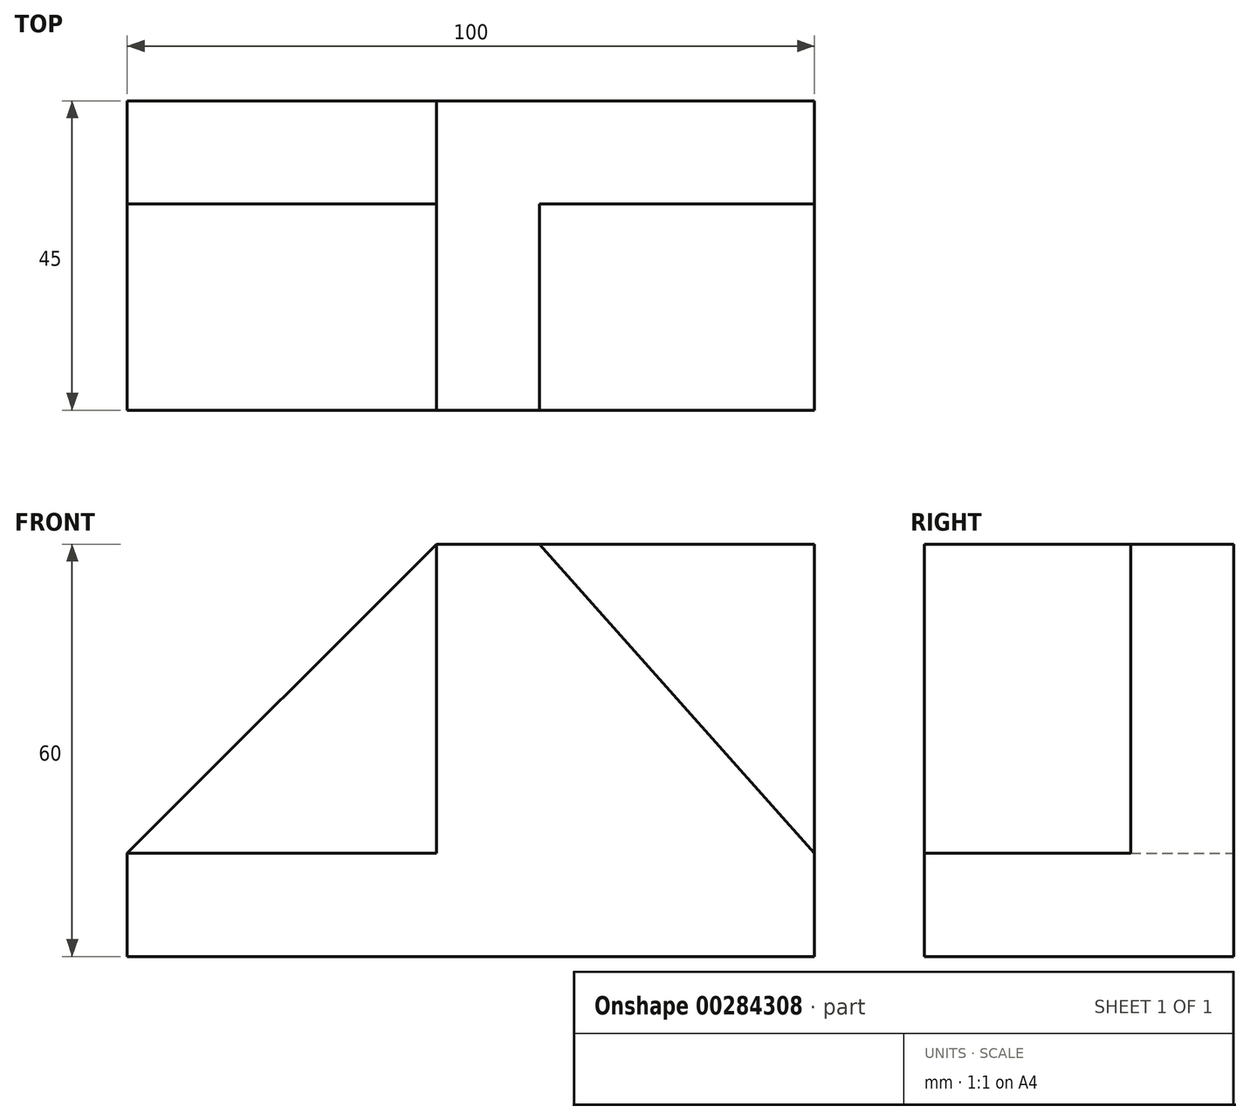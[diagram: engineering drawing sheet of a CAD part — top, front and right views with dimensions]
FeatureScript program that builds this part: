
annotation { "Feature Type Name" : "Feature", "Feature Type Description" : "" }
export const myFeature = defineFeature(function(context is Context, id is Id, definition is map)
    precondition{}
    {
        {
            var Q0;
            Q0=qCreatedBy(makeId("Front.planeOp"),FACE);
            var sketch = newSketch(context, id + "F0", { "sketchPlane" : qUnion([Q0])});
            skLineSegment(sketch, "E0", {"start": v(-62.69, -4.46) * mm, "end": v(-62.69, -19.46) * mm});
            skLineSegment(sketch, "E1", {"start": v(-62.69, -19.46) * mm, "end": v(37.31, -19.46) * mm});
            skLineSegment(sketch, "E2", {"start": v(37.31, -19.46) * mm, "end": v(37.31, -4.46) * mm});
            skLineSegment(sketch, "E3", {"start": v(-17.69, 40.54) * mm, "end": v(-2.69, 40.54) * mm});
            skLineSegment(sketch, "E4", {"start": v(-2.69, 40.54) * mm, "end": v(37.31, 40.54) * mm});
            skLineSegment(sketch, "E5", {"start": v(37.31, 40.54) * mm, "end": v(37.31, -4.46) * mm});
            skLineSegment(sketch, "E6", {"start": v(-62.69, -4.46) * mm, "end": v(-17.69, 40.54) * mm});
            skSolve(sketch);
        }
        {
            var Q0;
            Q0 = qSketchRegion(id + "F0", true);
            extrude(context, id + "F1", {"entities" : qUnion([Q0]), "depth" : 45 * mm});
        }
        {
            var Q0;
            Q0=makeQuery(id+"F1.opExtrude","CAP_FACE",FACE,{"disambiguationData":[OSD([sQuery(id+"F0.wireOp",EDGE,"E0"),sQuery(id+"F0.wireOp",EDGE,"E1"),sQuery(id+"F0.wireOp",EDGE,"E2"),sQuery(id+"F0.wireOp",EDGE,"E3"),sQuery(id+"F0.wireOp",EDGE,"E4"),sQuery(id+"F0.wireOp",EDGE,"E5"),sQuery(id+"F0.wireOp",EDGE,"E6")])],"isStart":false});
            var sketch = newSketch(context, id + "F2", { "sketchPlane" : qUnion([Q0])});
            skLineSegment(sketch, "E7", {"start": v(-17.69, 40.54) * mm, "end": v(-17.69, -4.46) * mm});
            skLineSegment(sketch, "E8", {"start": v(-17.69, -4.46) * mm, "end": v(-62.69, -4.46) * mm});
            skLineSegment(sketch, "E9", {"start": v(-62.69, -4.46) * mm, "end": v(-17.69, 40.54) * mm});
            skSolve(sketch);
        }
        {
            var Q0;
            Q0 = qSketchRegion(id + "F2", true);
            extrude(context, id + "F3", {"entities" : qUnion([Q0]), "operationType" : NewBodyOperationType.REMOVE, "oppositeDirection" : true, "depth" : 30 * mm});
        }
        {
            var Q0;
            Q0=makeQuery(id+"F1.opExtrude","CAP_FACE",FACE,{"disambiguationData":[OSD([sQuery(id+"F0.wireOp",EDGE,"E0"),sQuery(id+"F0.wireOp",EDGE,"E1"),sQuery(id+"F0.wireOp",EDGE,"E2"),sQuery(id+"F0.wireOp",EDGE,"E3"),sQuery(id+"F0.wireOp",EDGE,"E4"),sQuery(id+"F0.wireOp",EDGE,"E5"),sQuery(id+"F0.wireOp",EDGE,"E6")])],"isStart":false});
            var sketch = newSketch(context, id + "F4", { "sketchPlane" : qUnion([Q0])});
            skLineSegment(sketch, "E10", {"start": v(-2.69, 40.54) * mm, "end": v(37.31, -4.46) * mm});
            skLineSegment(sketch, "E11", {"start": v(37.31, 40.54) * mm, "end": v(-2.69, 40.54) * mm});
            skSolve(sketch);
        }
        {
            var Q0;
            Q0 = qSketchRegion(id + "F4", true);
            var Q1;
            {var subQ0=sQuery(id+"F4.wireOp",EDGE,"E10");Q1=makeQuery(id+"F4.imprint","IMPRINT",FACE,{"disambiguationData":[TD([[makeQuery(id+"F4.imprint","IMPRINT",EDGE,{"derivedFrom":subQ0}),1.0]])]});}
            extrude(context, id + "F5", {"entities" : qUnion([Q0, Q1]), "operationType" : NewBodyOperationType.REMOVE, "oppositeDirection" : true, "depth" : 30 * mm});
        }
    });
